# Revit family: 6223 22_Anschlussverschraubung
name_source: partatom
category: Rohrformteile
units: mm (PartAtom-declared; Revit-internal decimal feet)

## family parameters
Arbeitsebenenbasiert = Nein
Beim Laden mit Abzugskörper schneiden = Nein
Bemaßung runder Anschluss = Durchmesser verwenden
Gemeinsam genutzt = Nein
Immer vertikal = Ja
OmniClass-Nummer = 23.65.55.14
OmniClass-Titel = Valves for Liquid Services
Teiletyp = Verbindung

## types (1)
- G3/4xM22x1,5
    Anschlussstück = Messing CW614N, vernickelt
    Ausführung = Anschlussverschraubung, konisch dichtend mit freidrehender Überwurfmutter G3/4".
    Bestellnummer = 1622322
    Hersteller = HERZ Armaturen Ges.m.b.H.
    Hinweiß = Der O-Ring dient als zusätzliche Dichtung, bei Verlust ist die Anschlussverschraubung metallisch dichtend.
    Max. Betriebsdruck = 1000000.0 Pa
    Max. Betriebstemperatur = 110 °C
    Medium = Heizungswasser nach ÖNORM H5195 oder VDI- Richtlinie 2035.
Die Verwendung von Ethylen- oder Propyleneglykol in einem Mischungsverhältnis 25- 50% ist zulässig.
    Mutter = Messing CW614N, vernickelt
    O-Ring = EPDM
    S02 = 8 mm  [stored 0.0262467 ft]
    SCRNCODE = 07;01;02
    SCRNSEQ = AWI;AWI_TYP="1001";2
    URL = www.herz-armaturen.at
    Vorgabe-Ansicht = 0 mm  [stored 0 ft]

note: [stored X ft] marks values corroborated as IEEE doubles in the binary element streams (Revit-internal decimal feet)
